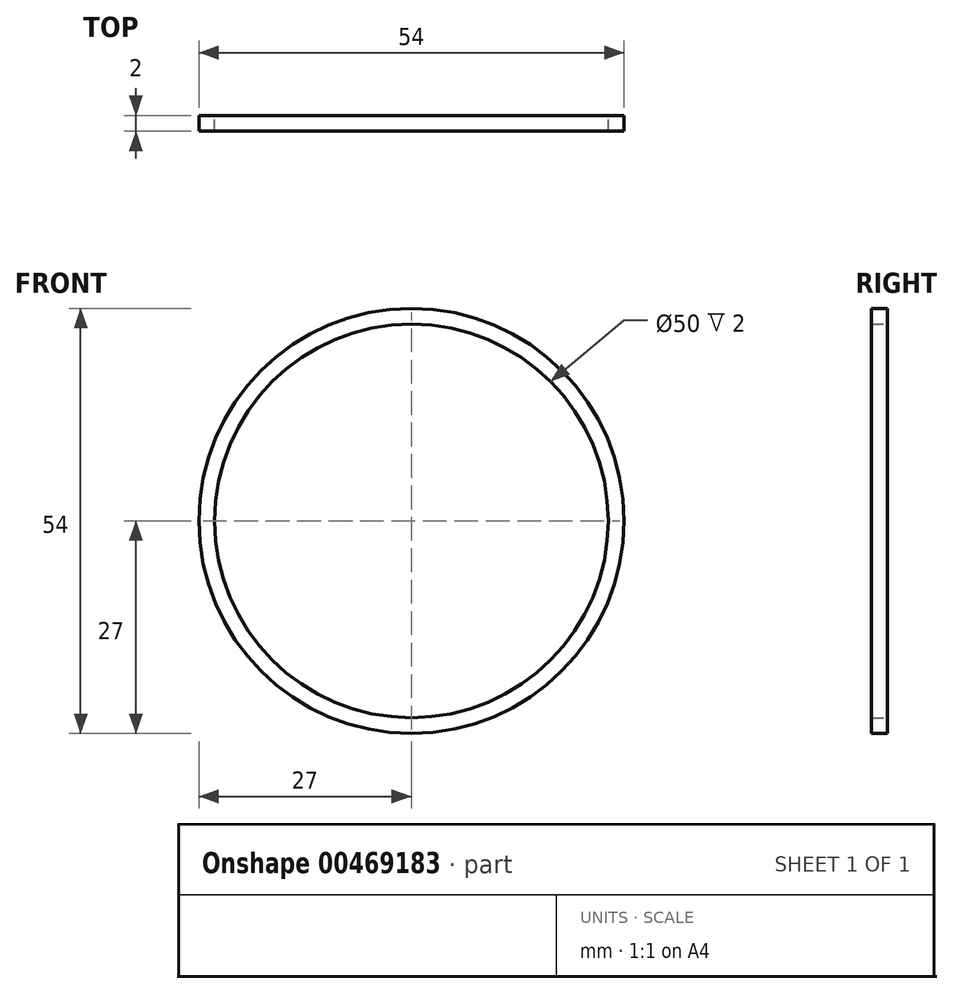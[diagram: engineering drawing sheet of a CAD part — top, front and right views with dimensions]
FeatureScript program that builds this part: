
annotation { "Feature Type Name" : "Feature", "Feature Type Description" : "" }
export const myFeature = defineFeature(function(context is Context, id is Id, definition is map)
    precondition{}
    {
        {
            var Q0;
            Q0=qCreatedBy(makeId("Front.planeOp"),FACE);
            var sketch = newSketch(context, id + "F0", { "sketchPlane" : qUnion([Q0])});
            skCircle(sketch, "E0", {"center": v(0, 0) * mm, "radius": 27 * mm});
            skCircle(sketch, "E1", {"center": v(0, 0) * mm, "radius": 25 * mm});
            skCircle(sketch, "E2", {"center": v(0, 0) * mm, "radius": 17 * mm});
            skCircle(sketch, "E3", {"center": v(0, 0) * mm, "radius": 15 * mm});
            skCircle(sketch, "E4", {"center": v(0, 0) * mm, "radius": 3.75 * mm});
            skLineSegment(sketch, "E5", {"start": v(0, 0) * mm, "end": v(-15, 0) * mm});
            skLineSegment(sketch, "E6", {"start": v(-17, 0) * mm, "end": v(-25, 0) * mm});
            skLineSegment(sketch, "E7.1.0", {"start": v(-16.17, -5.25) * mm, "end": v(-23.78, -7.73) * mm});
            skLineSegment(sketch, "E7.1.1", {"start": v(0, 0) * mm, "end": v(-14.27, -4.64) * mm});
            skLineSegment(sketch, "E7.2.0", {"start": v(-13.75, -10) * mm, "end": v(-20.23, -14.7) * mm});
            skLineSegment(sketch, "E7.2.1", {"start": v(0, 0) * mm, "end": v(-12.14, -8.82) * mm});
            skLineSegment(sketch, "E8.2.3.0", {"start": v(-10, -13.75) * mm, "end": v(-14.7, -20.23) * mm});
            skLineSegment(sketch, "E8.3.3.0", {"start": v(0, 0) * mm, "end": v(-8.82, -12.14) * mm});
            skLineSegment(sketch, "E8.2.4.0", {"start": v(-5.25, -16.17) * mm, "end": v(-7.73, -23.78) * mm});
            skLineSegment(sketch, "E8.3.4.0", {"start": v(0, 0) * mm, "end": v(-4.64, -14.27) * mm});
            skLineSegment(sketch, "E8.2.5.0", {"start": v(0, -17) * mm, "end": v(0, -25) * mm});
            skLineSegment(sketch, "E8.3.5.0", {"start": v(0, 0) * mm, "end": v(0, -15) * mm});
            skLineSegment(sketch, "E8.2.6.0", {"start": v(5.25, -16.17) * mm, "end": v(7.73, -23.78) * mm});
            skLineSegment(sketch, "E8.3.6.0", {"start": v(0, 0) * mm, "end": v(4.64, -14.27) * mm});
            skLineSegment(sketch, "E8.2.7.0", {"start": v(10, -13.75) * mm, "end": v(14.7, -20.23) * mm});
            skLineSegment(sketch, "E8.3.7.0", {"start": v(0, 0) * mm, "end": v(8.82, -12.14) * mm});
            skLineSegment(sketch, "E8.2.8.0", {"start": v(13.75, -10) * mm, "end": v(20.23, -14.7) * mm});
            skLineSegment(sketch, "E8.3.8.0", {"start": v(0, 0) * mm, "end": v(12.14, -8.82) * mm});
            skLineSegment(sketch, "E8.2.9.0", {"start": v(16.17, -5.25) * mm, "end": v(23.78, -7.73) * mm});
            skLineSegment(sketch, "E8.3.9.0", {"start": v(0, 0) * mm, "end": v(14.27, -4.64) * mm});
            skLineSegment(sketch, "E8.2.10.0", {"start": v(17, 0) * mm, "end": v(25, 0) * mm});
            skLineSegment(sketch, "E8.3.10.0", {"start": v(0, 0) * mm, "end": v(15, 0) * mm});
            skLineSegment(sketch, "E8.2.11.0", {"start": v(16.17, 5.25) * mm, "end": v(23.78, 7.73) * mm});
            skLineSegment(sketch, "E8.3.11.0", {"start": v(0, 0) * mm, "end": v(14.27, 4.64) * mm});
            skLineSegment(sketch, "E8.2.12.0", {"start": v(13.75, 10) * mm, "end": v(20.23, 14.7) * mm});
            skLineSegment(sketch, "E8.3.12.0", {"start": v(0, 0) * mm, "end": v(12.14, 8.82) * mm});
            skLineSegment(sketch, "E8.2.13.0", {"start": v(10, 13.75) * mm, "end": v(14.7, 20.23) * mm});
            skLineSegment(sketch, "E8.3.13.0", {"start": v(0, 0) * mm, "end": v(8.82, 12.14) * mm});
            skLineSegment(sketch, "E8.2.14.0", {"start": v(5.25, 16.17) * mm, "end": v(7.73, 23.78) * mm});
            skLineSegment(sketch, "E8.3.14.0", {"start": v(0, 0) * mm, "end": v(4.64, 14.27) * mm});
            skLineSegment(sketch, "E8.2.15.0", {"start": v(0, 17) * mm, "end": v(0, 25) * mm});
            skLineSegment(sketch, "E8.3.15.0", {"start": v(0, 0) * mm, "end": v(0, 15) * mm});
            skLineSegment(sketch, "E8.2.16.0", {"start": v(-5.25, 16.17) * mm, "end": v(-7.73, 23.78) * mm});
            skLineSegment(sketch, "E8.3.16.0", {"start": v(0, 0) * mm, "end": v(-4.64, 14.27) * mm});
            skLineSegment(sketch, "E8.2.17.0", {"start": v(-10, 13.75) * mm, "end": v(-14.7, 20.23) * mm});
            skLineSegment(sketch, "E8.3.17.0", {"start": v(0, 0) * mm, "end": v(-8.82, 12.14) * mm});
            skLineSegment(sketch, "E8.2.18.0", {"start": v(-13.75, 10) * mm, "end": v(-20.23, 14.7) * mm});
            skLineSegment(sketch, "E8.3.18.0", {"start": v(0, 0) * mm, "end": v(-12.14, 8.82) * mm});
            skLineSegment(sketch, "E8.2.19.0", {"start": v(-16.17, 5.25) * mm, "end": v(-23.78, 7.73) * mm});
            skLineSegment(sketch, "E8.3.19.0", {"start": v(0, 0) * mm, "end": v(-14.27, 4.64) * mm});
            skSolve(sketch);
        }
        {
            var Q0;
            Q0=makeQuery(id+"F0.imprint","IMPRINT",FACE,{"disambiguationData":[TD([[makeQuery(id+"F0.imprint","IMPRINT",EDGE,{"derivedFrom":sQuery(id+"F0.wireOp",EDGE,"E0")}),1.0]])]});
            extrude(context, id + "F1", {"entities" : qUnion([Q0]), "depth" : 2 * mm, "offsetDistance" : 25 * mm});
        }
    });
